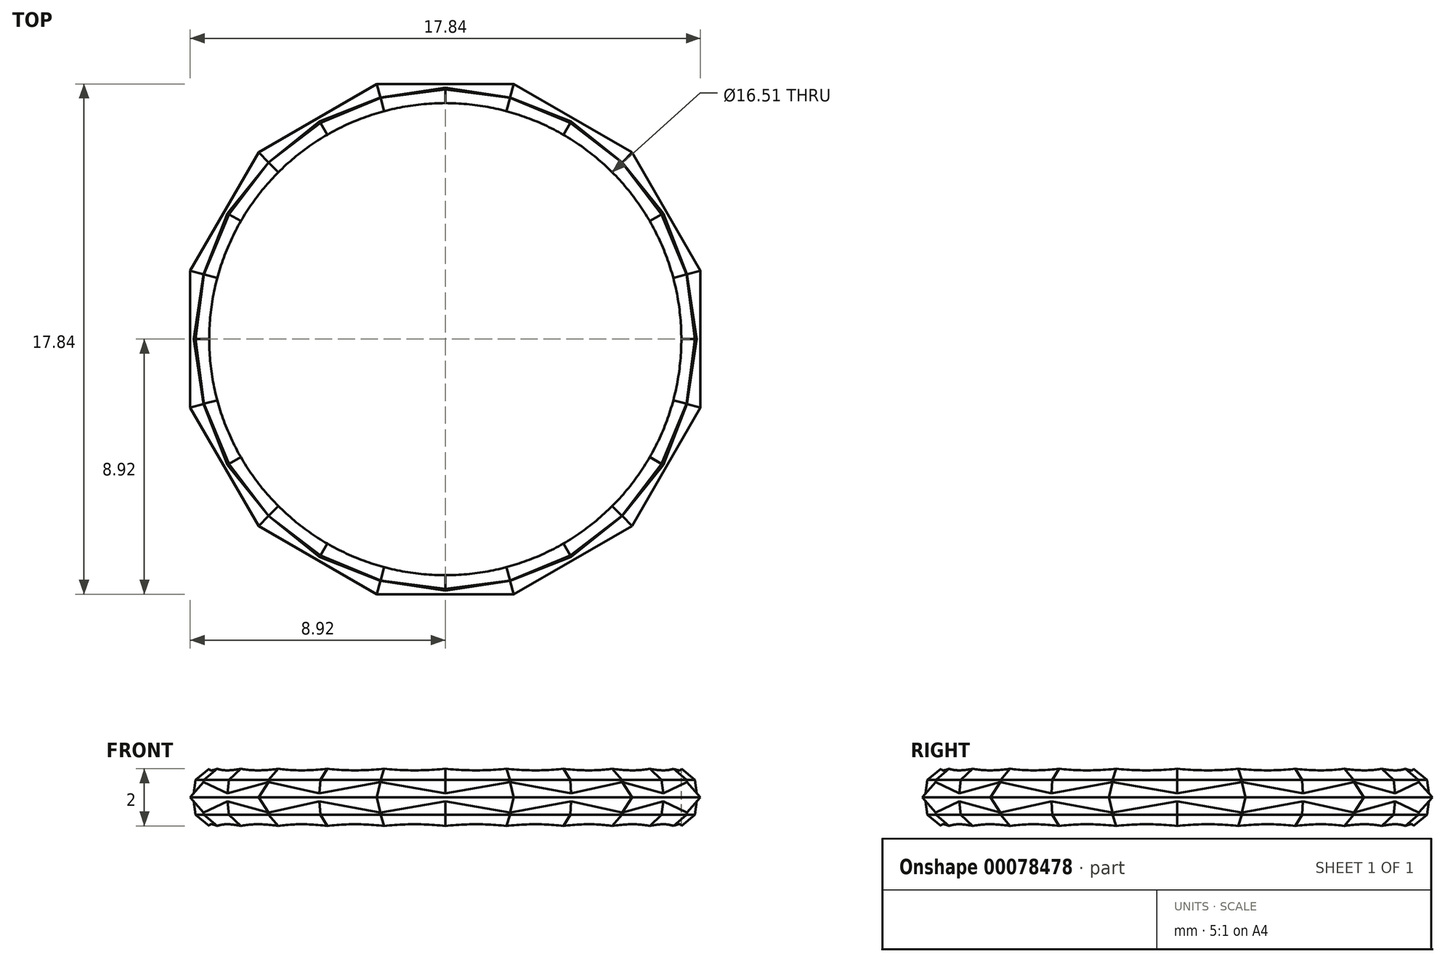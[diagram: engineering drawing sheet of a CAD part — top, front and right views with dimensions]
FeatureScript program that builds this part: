
annotation { "Feature Type Name" : "Feature", "Feature Type Description" : "" }
export const myFeature = defineFeature(function(context is Context, id is Id, definition is map)
    precondition{}
    {
        {
            var Q0;
            Q0=qCreatedBy(makeId("Top.planeOp"),FACE);
            var sketch = newSketch(context, id + "F0", { "sketchPlane" : qUnion([Q0])});
            skCircle(sketch, "E0", {"center": v(0, 0) * mm, "radius": 8.26 * mm});
            skLineSegment(sketch, "E1", {"start": v(0, 0) * mm, "end": v(-8.26, 0) * mm, "construction": true});
            skLineSegment(sketch, "E2", {"start": v(0, 0) * mm, "end": v(-7.97, 2.14) * mm, "construction": true});
            skSolve(sketch);
        }
        {
            var Q0;
            Q0=qCreatedBy(makeId("Front.planeOp"),FACE);
            var sketch = newSketch(context, id + "F1", { "sketchPlane" : qUnion([Q0])});
            skLineSegment(sketch, "E3", {"start": v(-8.26, 1) * mm, "end": v(-8.26, -1) * mm});
            skLineSegment(sketch, "E4", {"start": v(-8.26, 1) * mm, "end": v(-8.74, 0.61) * mm});
            skLineSegment(sketch, "E5", {"start": v(-8.74, 0.61) * mm, "end": v(-8.82, 0) * mm});
            skLineSegment(sketch, "E6", {"start": v(-8.82, 0) * mm, "end": v(-8.74, -0.61) * mm});
            skLineSegment(sketch, "E7", {"start": v(-8.74, -0.61) * mm, "end": v(-8.26, -1) * mm});
            skLineSegment(sketch, "E8", {"start": v(-8.82, 0) * mm, "end": v(-8.26, 0) * mm, "construction": true});
            skSolve(sketch);
        }
        {
            var Q0;
            Q0=qCreatedBy(makeId("Top.planeOp"),FACE);
            var sketch = newSketch(context, id + "F2", { "sketchPlane" : qUnion([Q0])});
            skCircle(sketch, "E9.cCircle", {"center": v(0, 0) * mm, "radius": 8.2 * mm, "construction": true});
            skLineSegment(sketch, "E9.0", {"start": v(-8.2, 0) * mm, "end": v(-7.92, 2.12) * mm});
            skLineSegment(sketch, "E9.1", {"start": v(-7.92, 2.12) * mm, "end": v(-7.1, 4.1) * mm});
            skLineSegment(sketch, "E9.2", {"start": v(-7.1, 4.1) * mm, "end": v(-5.8, 5.8) * mm});
            skLineSegment(sketch, "E9.3", {"start": v(-5.8, 5.8) * mm, "end": v(-4.1, 7.1) * mm});
            skLineSegment(sketch, "E9.4", {"start": v(-4.1, 7.1) * mm, "end": v(-2.12, 7.92) * mm});
            skLineSegment(sketch, "E9.5", {"start": v(-2.12, 7.92) * mm, "end": v(0, 8.2) * mm});
            skLineSegment(sketch, "E9.6", {"start": v(0, 8.2) * mm, "end": v(2.12, 7.92) * mm});
            skLineSegment(sketch, "E9.7", {"start": v(2.12, 7.92) * mm, "end": v(4.1, 7.1) * mm});
            skLineSegment(sketch, "E9.8", {"start": v(4.1, 7.1) * mm, "end": v(5.8, 5.8) * mm});
            skLineSegment(sketch, "E9.9", {"start": v(5.8, 5.8) * mm, "end": v(7.1, 4.1) * mm});
            skLineSegment(sketch, "E9.10", {"start": v(7.1, 4.1) * mm, "end": v(7.92, 2.12) * mm});
            skLineSegment(sketch, "E9.11", {"start": v(7.92, 2.12) * mm, "end": v(8.2, 0) * mm});
            skLineSegment(sketch, "E9.12", {"start": v(8.2, 0) * mm, "end": v(7.92, -2.12) * mm});
            skLineSegment(sketch, "E9.13", {"start": v(7.92, -2.12) * mm, "end": v(7.1, -4.1) * mm});
            skLineSegment(sketch, "E9.14", {"start": v(7.1, -4.1) * mm, "end": v(5.8, -5.8) * mm});
            skLineSegment(sketch, "E9.15", {"start": v(5.8, -5.8) * mm, "end": v(4.1, -7.1) * mm});
            skLineSegment(sketch, "E9.16", {"start": v(4.1, -7.1) * mm, "end": v(2.12, -7.92) * mm});
            skLineSegment(sketch, "E9.17", {"start": v(2.12, -7.92) * mm, "end": v(0, -8.2) * mm});
            skLineSegment(sketch, "E9.18", {"start": v(0, -8.2) * mm, "end": v(-2.12, -7.92) * mm});
            skLineSegment(sketch, "E9.19", {"start": v(-2.12, -7.92) * mm, "end": v(-4.1, -7.1) * mm});
            skLineSegment(sketch, "E9.20", {"start": v(-4.1, -7.1) * mm, "end": v(-5.8, -5.8) * mm});
            skLineSegment(sketch, "E9.21", {"start": v(-5.8, -5.8) * mm, "end": v(-7.1, -4.1) * mm});
            skLineSegment(sketch, "E9.22", {"start": v(-7.1, -4.1) * mm, "end": v(-7.92, -2.12) * mm});
            skLineSegment(sketch, "E9.23", {"start": v(-7.92, -2.12) * mm, "end": v(-8.2, 0) * mm});
            skLineSegment(sketch, "E10", {"start": v(0, 0) * mm, "end": v(-8.2, 0) * mm, "construction": true});
            skSolve(sketch);
        }
        {
            var Q0;
            Q0 = qSketchRegion(id + "F1", true);
            var Q1;
            Q1 = qConstructionFilter(qBodyType(qCreatedBy(id + "F2" ,EDGE), BodyType.WIRE), ConstructionObject.NO);
            sweep(context, id + "F3", {"profiles" : qUnion([Q0]), "path" : qUnion([Q1])});
        }
        {
            var Q0;
            Q0=makeQuery(id+"F3.opSweep","SWEPT_FACE",FACE,{"disambiguationData":[OSD([sQuery(id+"F1.wireOp",EDGE,"E3"),sQuery(id+"F2.wireOp",EDGE,"E9.0")])]});
            var sketch = newSketch(context, id + "F4", { "sketchPlane" : qUnion([Q0])});
            skPoint(sketch, "E11.middle", {"position": v(0, 0) * mm});
            skLineSegment(sketch, "E12", {"start": v(-0.67, 0) * mm, "end": v(0, 0.43) * mm});
            skLineSegment(sketch, "E13", {"start": v(0, 0.43) * mm, "end": v(0.67, 0) * mm});
            skLineSegment(sketch, "E14", {"start": v(0.67, 0) * mm, "end": v(0, -0.43) * mm});
            skLineSegment(sketch, "E15", {"start": v(0, -0.43) * mm, "end": v(-0.67, 0) * mm});
            skLineSegment(sketch, "E16", {"start": v(0, 0.43) * mm, "end": v(0, -0.43) * mm, "construction": true});
            skSolve(sketch);
        }
        {
            var Q0;
            Q0=qCreatedBy(makeId("Front.planeOp"),FACE);
            var sketch = newSketch(context, id + "F5", { "sketchPlane" : qUnion([Q0])});
            skLineSegment(sketch, "E17", {"start": v(-8.26, 1) * mm, "end": v(-8.26, -1) * mm});
            skLineSegment(sketch, "E18.bottom", {"start": v(-8.26, 1) * mm, "end": v(-7.75, 1) * mm});
            skLineSegment(sketch, "E18.top", {"start": v(-8.26, -1) * mm, "end": v(-7.75, -1) * mm});
            skLineSegment(sketch, "E18.right", {"start": v(-7.75, 1) * mm, "end": v(-7.75, -1) * mm});
            skSolve(sketch);
        }
        {
            var Q0;
            Q0 = qSketchRegion(id + "F5", true);
            var Q1;
            Q1 = qConstructionFilter(qBodyType(qCreatedBy(id + "F0" ,EDGE), BodyType.WIRE), ConstructionObject.NO);
            sweep(context, id + "F6", {"operationType" : NewBodyOperationType.REMOVE, "profiles" : qUnion([Q0]), "path" : qUnion([Q1])});
        }
        {
            var Q0;
            Q0=qCreatedBy(makeId("Top.planeOp"),FACE);
            var sketch = newSketch(context, id + "F7", { "sketchPlane" : qUnion([Q0])});
            skCircle(sketch, "E19.cCircle", {"center": v(0, 0) * mm, "radius": 8.26 * mm, "construction": true});
            skLineSegment(sketch, "E19.0", {"start": v(-8.25, -2.21) * mm, "end": v(-8.25, 2.21) * mm});
            skLineSegment(sketch, "E19.1", {"start": v(-8.25, 2.21) * mm, "end": v(-6.04, 6.04) * mm});
            skLineSegment(sketch, "E19.2", {"start": v(-6.04, 6.04) * mm, "end": v(-2.21, 8.25) * mm});
            skLineSegment(sketch, "E19.3", {"start": v(-2.21, 8.25) * mm, "end": v(2.21, 8.25) * mm});
            skLineSegment(sketch, "E19.4", {"start": v(2.21, 8.26) * mm, "end": v(6.04, 6.04) * mm});
            skLineSegment(sketch, "E19.5", {"start": v(6.04, 6.04) * mm, "end": v(8.25, 2.21) * mm});
            skLineSegment(sketch, "E19.6", {"start": v(8.25, 2.21) * mm, "end": v(8.25, -2.21) * mm});
            skLineSegment(sketch, "E19.7", {"start": v(8.25, -2.21) * mm, "end": v(6.04, -6.04) * mm});
            skLineSegment(sketch, "E19.8", {"start": v(6.04, -6.04) * mm, "end": v(2.21, -8.25) * mm});
            skLineSegment(sketch, "E19.9", {"start": v(2.21, -8.25) * mm, "end": v(-2.21, -8.25) * mm});
            skLineSegment(sketch, "E19.10", {"start": v(-2.21, -8.25) * mm, "end": v(-6.04, -6.04) * mm});
            skLineSegment(sketch, "E19.11", {"start": v(-6.04, -6.04) * mm, "end": v(-8.25, -2.21) * mm});
            skPoint(sketch, "E19.0.midPoint", {"position": v(-8.26, 0) * mm});
            skLineSegment(sketch, "E20", {"start": v(0, 0) * mm, "end": v(-8.26, 0) * mm, "construction": true});
            skSolve(sketch);
        }
        {
            var Q0;
            Q0=qCreatedBy(makeId("Front.planeOp"),FACE);
            var sketch = newSketch(context, id + "F8", { "sketchPlane" : qUnion([Q0])});
            skLineSegment(sketch, "E21", {"start": v(-8.26, 0.75) * mm, "end": v(-8.26, -0.75) * mm});
            skLineSegment(sketch, "E22", {"start": v(-8.26, 0.75) * mm, "end": v(-8.92, 0) * mm});
            skLineSegment(sketch, "E23", {"start": v(-8.92, 0) * mm, "end": v(-8.26, -0.75) * mm});
            skPoint(sketch, "E24", {"position": v(-8.59, 0.38) * mm});
            skPoint(sketch, "E25", {"position": v(-8.59, -0.38) * mm});
            skSolve(sketch);
        }
        {
            var Q0;
            Q0 = qSketchRegion(id + "F8", true);
            var Q1;
            Q1 = qConstructionFilter(qBodyType(qCreatedBy(id + "F7" ,EDGE), BodyType.WIRE), ConstructionObject.NO);
            sweep(context, id + "F9", {"operationType" : NewBodyOperationType.ADD, "profiles" : qUnion([Q0]), "path" : qUnion([Q1])});
        }
    });
